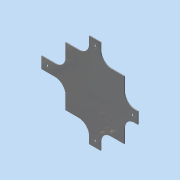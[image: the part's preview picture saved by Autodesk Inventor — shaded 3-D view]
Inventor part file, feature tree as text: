
AUTODESK INVENTOR PART (.ipt)
format: ipt  version: 2015 (Build 190159000, 159)  size: 313,856 bytes
history: native  units: in
note: dims shown in document units (in); Inventor stores cm internally (conversion verified against a paired STEP export)
features: sketch x21, projected_geometry x16, extrude x11, hole x10, pattern_circular x4, chamfer x2, plane x2
ambient origin geometry x8: Origin, YZ Plane, XZ Plane, XY Plane, X Axis, Y Axis, Z Axis, Center Point
bodies: Solid1 (feature_tree)
feature tree (66):
  extrude  "Extrusion1"  Depth=11.811in
  hole  "Hole1"  [1 undecoded]
  hole  "Hole2"  [1 undecoded]
  hole  "Hole3"  [1 undecoded]
  chamfer  "Chamfer1"  Distance=0.125in Angle=45.0deg
  chamfer  "Chamfer2"  Distance=0.125in Angle=45.0deg
  sketch  "Sketch5"  dims[d9=0.2756in]
  extrude  "Extrusion2"  Depth=5.9055in
  plane  "Work Plane1"
  extrude  "Extrusion3"  Depth=5.9055in
  plane  "Work Plane2"
  extrude  "Extrusion4"  Depth=0.1575in TaperAngle=360.0deg
  extrude  "Extrusion5"  Depth=0.1575in TaperAngle=0.0deg
  hole  "Hole5"  [1 undecoded]
  extrude  "Extrusion6"  Depth=0.1575in TaperAngle=0.0deg
  hole  "Hole6"  [1 undecoded]
  extrude  "Extrusion7"  Depth=0.1575in
  hole  "Hole7"  [1 undecoded]
  extrude  "Extrusion8"  Depth=0.1575in TaperAngle=0.0deg
  extrude  "Extrusion9"  Depth=0.1575in
  extrude  "Extrusion10"  Depth=0.1575in
  extrude  "Extrusion11"  Depth=0.1575in TaperAngle=0.0deg
  hole  "Hole8"  [1 undecoded]
  pattern_circular  "Circular Pattern2"  [2 undecoded]
  hole  "Hole9"  [1 undecoded]
  pattern_circular  "Circular Pattern3"  [2 undecoded]
  hole  "Hole10"  [1 undecoded]
  pattern_circular  "Circular Pattern4"  [2 undecoded]
  hole  "Hole11"  [1 undecoded]
  pattern_circular  "Circular Pattern5"  [2 undecoded]
  sketch  "Sketch1"  dims[d0=11.811in d1=11.811in]
  sketch  "Sketch2"  dims[d2=0.125in d3=0.0in d4=0.2756in]
  sketch  "Sketch3"  dims[d5=0.2756in d6=0.2756in]
  sketch  "Sketch4"  dims[d7=0.2756in d8=0.2756in]
  projected_geometry  "Projected Loop1"
  sketch  "Sketch6"  dims[d10=0.2756in]
  projected_geometry  "Projected Loop2"
  projected_geometry  "Projected Loop3"
  projected_geometry  "Projected Loop4"
  projected_geometry  "Projected Loop5"
  projected_geometry  "Projected Loop6"
  projected_geometry  "Projected Loop7"
  projected_geometry  "Projected Loop8"
  sketch  "Sketch7"  dims[d11=0.2756in]
  projected_geometry  "Projected Loop9"
  sketch  "Sketch8"  dims[d12=0.315in d13=0.75in d14=0.375in d15=0.25in d16=0.5635in d17=1.0in d18=0.8108in]
  projected_geometry  "Projected Loop10"
  sketch  "Sketch9"  dims[d19=8.189in]
  sketch  "Sketch10"  dims[d20=8.189in]
  projected_geometry  "Projected Loop11"
  sketch  "Sketch11"  dims[d21=8.189in]
  sketch  "Sketch12"  dims[d22=1.811in]
  projected_geometry  "Projected Loop12"
  sketch  "Sketch13"  dims[d23=1.811in]
  sketch  "Sketch14"  dims[d24=1.811in]
  projected_geometry  "Projected Loop13"
  sketch  "Sketch15"  dims[d25=8.189in]
  projected_geometry  "Projected Loop14"
  sketch  "Sketch16"  dims[d26=1.811in]
  projected_geometry  "Projected Loop15"
  sketch  "Sketch17"  dims[d27=0.1181in d28=0.75in d29=0.375in d30=0.25in d31=0.5635in d32=1.0in d33=0.8108in]
  projected_geometry  "Projected Loop16"
  sketch  "Sketch18"  dims[d38=0.2756in]
  sketch  "Sketch19"  dims[d41=5.9055in]
  sketch  "Sketch20"  dims[d42=0.315in d43=0.75in d44=0.375in d45=0.25in d46=0.5635in d47=1.0in d48=0.8108in d50=2.9528in d51=0.125in d52=45.0deg d53=2.0866in d54=0.125in d55=45.0deg]
  sketch  "Sketch21"  dims[d56=1.9685in d57=5.9055in d58=5.9055in d59=1.5748in d61=360.0deg d63=1.0in d64=0.0in d75=1.0in d76=0.0in d77=1.0in d78=0.0in d79=1.5748in d80=0.0in d81=0.8661in d82=0.2756in d83=0.315in d84=0.75in d85=0.375in d86=0.25in d87=0.5635in d88=1.0in d89=0.8108in d90=0.5906in d91=0.0in d92=0.2756in d93=0.8661in d94=0.315in d95=0.75in d96=0.375in d97=0.25in d98=0.5635in d99=1.0in d100=0.8108in d101=0.5906in d102=0.0in d103=0.8661in d104=0.2756in d105=0.315in d106=0.75in d107=0.375in d108=0.25in d109=0.5635in d110=1.0in d111=0.8108in d112=0.5906in d113=0.0in d114=0.5906in d115=0.0in d116=0.5906in d117=0.0in d118=0.5906in d119=0.0in d120=0.315in d121=0.8661in d122=0.1181in d123=0.2362in d124=0.1575in d125=0.0787in d126=90.0deg d127=0.315in d128=0.8108in d129=1.5748in d130=360.0deg d132=0.315in d133=0.8661in d134=0.1181in d135=0.2362in d136=0.1575in d137=0.0787in d138=90.0deg d139=0.315in d140=0.8108in d141=1.5748in d142=360.0deg d144=0.315in d145=0.8661in d146=0.1181in d147=0.2362in d148=0.1575in d149=0.0787in d150=90.0deg d151=0.315in d152=0.8108in d153=1.5748in d154=360.0deg d156=0.315in d157=0.1181in d158=0.2362in d159=0.1575in d160=0.0787in d161=90.0deg d162=0.315in d163=0.8108in d164=1.5748in d165=360.0deg]
note: 18 required parameter values undecoded (feature->parameter linkage not recoverable at this tier; creation-order binding heuristic only, values carry confidence <= 0.55)
